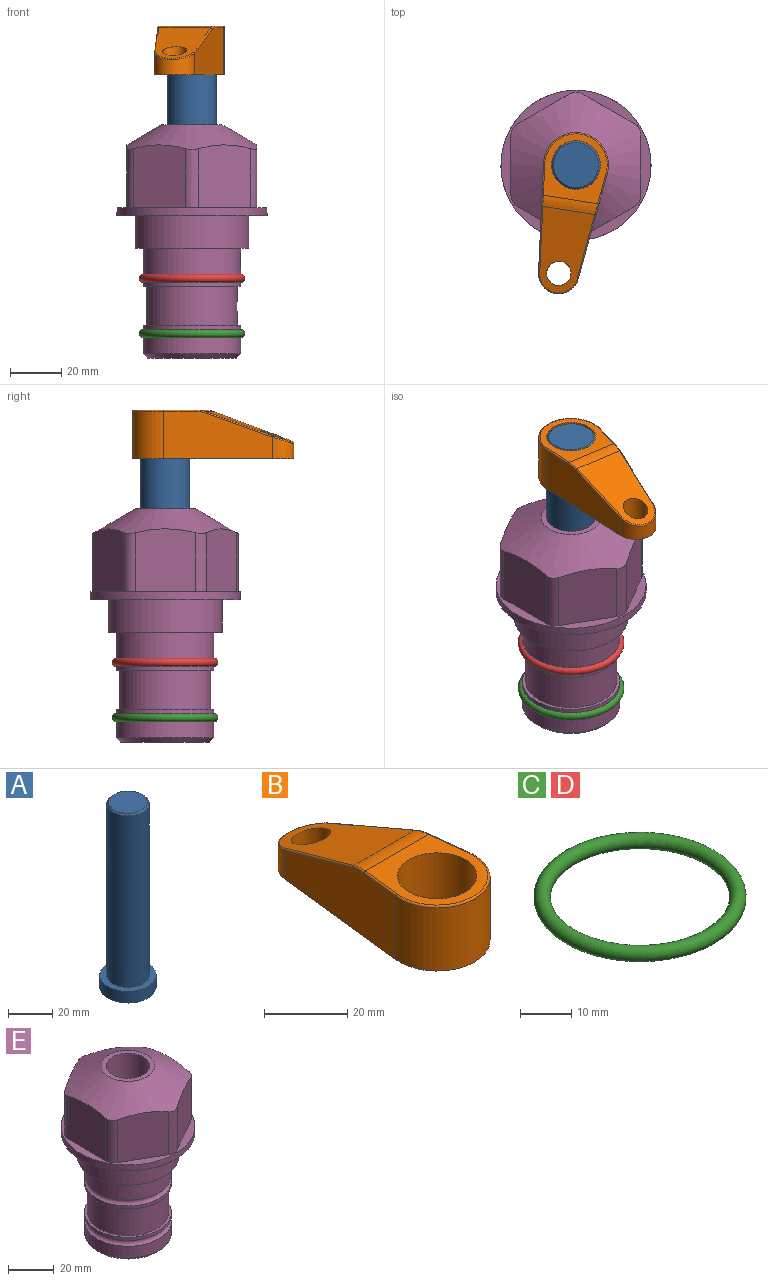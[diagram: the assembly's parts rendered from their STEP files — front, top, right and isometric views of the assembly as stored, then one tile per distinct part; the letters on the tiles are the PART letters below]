
ASSEMBLY  parts=5 mates=3
PART A: 6 faces, bbox 25.4x25.4x101.6 mm
  f0: plane 17.46x17.46mm, normal (0,0,1), area 239.5mm2, adj f5
  f1: plane 25.4x25.4mm, normal (0,0,-1), area 506.7mm2, adj f2
  f2: cylinder r=12.7mm len=25.4mm, axis (0,0,1), area 506.7mm2, adj f1,f3
  f3: plane 25.4x25.4mm, normal (0,0,1), area 221.7mm2, adj f2,f4
  f4: cylinder r=9.53mm len=94.46mm, axis (0,0,1), area 5653mm2, adj f3,f5
  f5: cone r=8.73mm half-angle=45deg, axis (0,0,-1), area 64.4mm2, adj f0,f4
PART B: 44 faces, bbox 27.5x64.5x19.1 mm
  f0: plane 2.3x0.95mm, normal (0,0,-1), area 1mm2, adj f25,f30,f34
  f1: plane 63.5x25.4mm, normal (0,0,-1), area 561.7mm2, adj f2,f3,f4,f5,f6,f7,f19,f20
  f2: cylinder r=12.7mm len=25.4mm, axis (0,0,-1), area 792.2mm2, adj f1,f3,f5,f13
  f3: plane 42.33x18.54mm, normal (0.99,0.11,0), area 647mm2, adj f1,f2,f4,f11,f12,f14
  f4: cylinder r=7.94mm len=15.78mm, axis (0,0,-1), area 158.6mm2, adj f1,f3,f5,f16
  f5: plane 42.33x18.54mm, normal (-0.99,0.11,0), area 647mm2, adj f1,f2,f4,f15,f17,f18
  f6: cylinder r=9.53mm len=19.05mm, axis (0,0,-1), area 1140.1mm2, adj f1,f8
  f7: cylinder r=4.76mm len=10.98mm, axis (0,0,-1), area 276.1mm2, adj f1,f9
  f8: plane 25.83x24.38mm, normal (0,0,1), area 262.2mm2, adj f6,f10,f11,f13,f15
  f9: plane 32.49x20.55mm, normal (0,0.34,0.94), area 489.9mm2, adj f7,f10,f14,f16,f18
  f10: cylinder r=12.7mm len=21.49mm, axis (-1,0,0), area 93.2mm2, adj f8,f9,f12,f17
  f11: cylinder r=0.51mm len=12.34mm, axis (0.11,-0.99,0), area 9.9mm2, adj f3,f8,f12,f13
  f12: bspline ~7.62x1.64mm, area 3.5mm2, adj f3,f10,f11,f14
  f13: torus R=12.19mm, axis (0,0,1), area 33.6mm2, adj f2,f8,f11,f15
  f14: cylinder r=0.51mm len=26.01mm, axis (0.1,-0.93,0.34), area 21.6mm2, adj f3,f9,f12,f16
  f15: cylinder r=0.51mm len=12.34mm, axis (0.11,0.99,0), area 9.9mm2, adj f5,f8,f13,f17
  f16: bspline ~15.78x7.05mm, area 15.7mm2, adj f4,f9,f14,f18
  f17: bspline ~7.62x1.64mm, area 3.5mm2, adj f5,f10,f15,f18
  f18: cylinder r=0.51mm len=26.01mm, axis (0.1,0.93,-0.34), area 21.6mm2, adj f5,f9,f16,f17
  f19: plane 21.6x14.29mm, normal (-0.99,-0.11,0), area 242.6mm2, adj f1,f26,f28,f34,f36,f38
  f20: plane 21.6x14.29mm, normal (0.99,-0.11,0), area 242.6mm2, adj f1,f27,f29,f37,f39,f41
  f21: cylinder r=12.7mm len=14.29mm, axis (0,0,-1), area 173.2mm2, adj f1,f26,f27,f30,f31,f33
  f22: cylinder r=7.94mm len=7.63mm, axis (0,0,-1), area 53.8mm2, adj f1,f28,f29,f42
  f23: plane 2.3x0.95mm, normal (0,0,-1), area 1mm2, adj f25,f33,f37
  f24: plane 17.94x12.32mm, normal (0,-0.34,-0.94), area 191.2mm2, adj f25,f38,f41,f42
  f25: cylinder r=9.53mm len=12.93mm, axis (-1,0,0), area 37.5mm2, adj f0,f23,f24,f31,f36,f39
  f26: cylinder r=1.59mm len=14.29mm, axis (0,0,-1), area 49mm2, adj f1,f19,f21,f32
  f27: cylinder r=1.59mm len=14.29mm, axis (0,0,-1), area 49mm2, adj f1,f20,f21,f35
  f28: cylinder r=1.59mm len=7.28mm, axis (0,0,-1), area 22.1mm2, adj f1,f19,f22,f40
  f29: cylinder r=1.59mm len=7.28mm, axis (0,0,-1), area 22.1mm2, adj f1,f20,f22,f43
  f30: torus R=14.29mm, axis (0,0,1), area 5.8mm2, adj f0,f21,f31,f32
  f31: bspline ~11.06x2.73mm, area 20.8mm2, adj f21,f25,f30,f33
  f32: sphere r=1.59mm, area 5.4mm2, adj f26,f30,f34
  f33: torus R=14.29mm, axis (0,0,1), area 5.8mm2, adj f21,f23,f31,f35
  f34: cylinder r=1.59mm len=1.68mm, axis (-0.11,0.99,0), area 2.4mm2, adj f0,f19,f32,f36
  f35: sphere r=1.59mm, area 5.4mm2, adj f27,f33,f37
  f36: bspline ~5.82x2.33mm, area 7.7mm2, adj f19,f25,f34,f38
  f37: cylinder r=1.59mm len=1.68mm, axis (0.11,0.99,0), area 2.4mm2, adj f20,f23,f35,f39
  f38: cylinder r=1.59mm len=18.33mm, axis (0.1,-0.93,0.34), area 46.7mm2, adj f19,f24,f36,f40
  f39: bspline ~5.82x2.33mm, area 7.7mm2, adj f20,f25,f37,f41
  f40: sphere r=1.59mm, area 3.6mm2, adj f28,f38,f42
  f41: cylinder r=1.59mm len=18.33mm, axis (0.1,0.93,-0.34), area 46.7mm2, adj f20,f24,f39,f43
  f42: bspline ~8.31x1.84mm, area 15.3mm2, adj f22,f24,f40,f43
  f43: sphere r=1.59mm, area 3.6mm2, adj f29,f41,f42
PART C: 1 faces, bbox 44.7x44.7x3.2 mm
  f0: torus R=19.05mm, axis (0,0,1), area 1193.9mm2
PART D: same geometry as C
PART E: 36 faces, bbox 58.7x58.7x91.2 mm
  f0: cylinder r=17.78mm len=35.56mm, axis (0,0,1), area 1670.8mm2, adj f23,f24,f31
  f1: cylinder r=19.05mm len=38.1mm, axis (0,0,1), area 1191.9mm2, adj f26,f27,f30
  f2: plane 58.66x58.66mm, normal (0,0,-1), area 1150.6mm2, adj f3,f28
  f3: cylinder r=29.33mm len=58.66mm, axis (0,0,-1), area 585.1mm2, adj f2,f4
  f4: plane 58.66x58.66mm, normal (0,0,1), area 475.9mm2, adj f3,f5,f6,f7,f8,f9,f10,f11
  f5: plane 24.5x20.32mm, normal (-0.5,0.87,0), area 562.8mm2, adj f4,f15,f16,f17
  f6: plane 24.5x20.32mm, normal (0.5,0.87,0), area 562.8mm2, adj f4,f14,f15,f17
  f7: plane 24.5x23.48mm, normal (1,0,0), area 562.8mm2, adj f4,f13,f14,f17
  f8: plane 24.5x20.32mm, normal (0.5,-0.87,0), area 562.8mm2, adj f4,f12,f13,f17
  f9: plane 24.5x20.32mm, normal (-0.5,-0.87,0), area 562.8mm2, adj f4,f11,f12,f17
  f10: plane 24.5x23.48mm, normal (-1,0,0), area 562.8mm2, adj f4,f11,f16,f17
  f11: cylinder r=5.08mm len=23.01mm, axis (0,0,-1), area 121.2mm2, adj f4,f9,f10,f17
  f12: cylinder r=5.08mm len=23.01mm, axis (0,0,-1), area 121.2mm2, adj f4,f8,f9,f17
  f13: cylinder r=5.08mm len=23.01mm, axis (0,0,-1), area 121.2mm2, adj f4,f7,f8,f17
  f14: cylinder r=5.08mm len=23.01mm, axis (0,0,-1), area 121.2mm2, adj f4,f6,f7,f17
  f15: cylinder r=5.08mm len=23.01mm, axis (0,0,-1), area 121.2mm2, adj f4,f5,f6,f17
  f16: cylinder r=5.08mm len=23.01mm, axis (0,0,-1), area 121.2mm2, adj f4,f5,f10,f17
  f17: cone r=11.73mm half-angle=60deg, axis (0,0,-1), area 2071.8mm2, adj f5,f6,f7,f8,f9,f10,f11,f12
  f18: plane 23.46x23.46mm, normal (0,0,1), area 147.4mm2, adj f17,f35
  f19: plane 34.93x34.93mm, normal (0,0,-1), area 958mm2, adj f29
  f20: cylinder r=19.05mm len=38.1mm, axis (0,0,1), area 760.1mm2, adj f21,f29
  f21: torus R=19.05mm, axis (0,0,1), area 565.3mm2, adj f20,f22
  f22: cylinder r=19.05mm len=38.1mm, axis (0,0,1), area 190mm2, adj f21,f23
  f23: plane 38.1x38.1mm, normal (0,0,1), area 146.9mm2, adj f0,f22
  f24: plane 38.1x38.1mm, normal (0,0,-1), area 146.9mm2, adj f0,f25
  f25: cylinder r=19.05mm len=38.1mm, axis (0,0,1), area 190mm2, adj f24,f26
  f26: torus R=19.05mm, axis (0,0,1), area 565.3mm2, adj f1,f25
  f27: plane 44.45x44.45mm, normal (0,0,-1), area 411.7mm2, adj f1,f28
  f28: cylinder r=22.23mm len=44.45mm, axis (0,0,1), area 1773.5mm2, adj f2,f27
  f29: cone r=19.05mm half-angle=45deg, axis (0,0,1), area 257.5mm2, adj f19,f20
  f30: cylinder r=3.17mm len=6.75mm, axis (-1,0,0), area 128mm2, adj f1,f33
  f31: cylinder r=3.17mm len=6.35mm, axis (-1,0,0), area 102.5mm2, adj f0,f33
  f32: plane 25.4x25.4mm, normal (0,0,1), area 506.7mm2, adj f33
  f33: cylinder r=12.7mm len=66.42mm, axis (0,0,-1), area 5236.2mm2, adj f30,f31,f32,f34
  f34: cone r=9.53mm half-angle=30deg, axis (0,0,-1), area 443.4mm2, adj f33,f35
  f35: cylinder r=9.53mm len=19.05mm, axis (0,0,-1), area 849mm2, adj f18,f34
PLACE A rot(axis=(0,0,-1),99deg) t=(0,0,0.44)mm
PLACE B rot(axis=(0,0,1),171deg) t=(0,0,55.05)mm
PLACE C t=(0,0,-21.59)mm
PLACE D at identity
PLACE E at identity fixed
MATE fastened C.f0 <-> E.f0  axis (0,0,1) through (0,0,-46.1)mm
MATE cylindrical A.f2 <-> E.f0  axis (0,0,1) through (0,0,26.08)mm
MATE fastened B.f2 <-> A.f2  axis (0,0,1) through (0,0,74.1)mm
